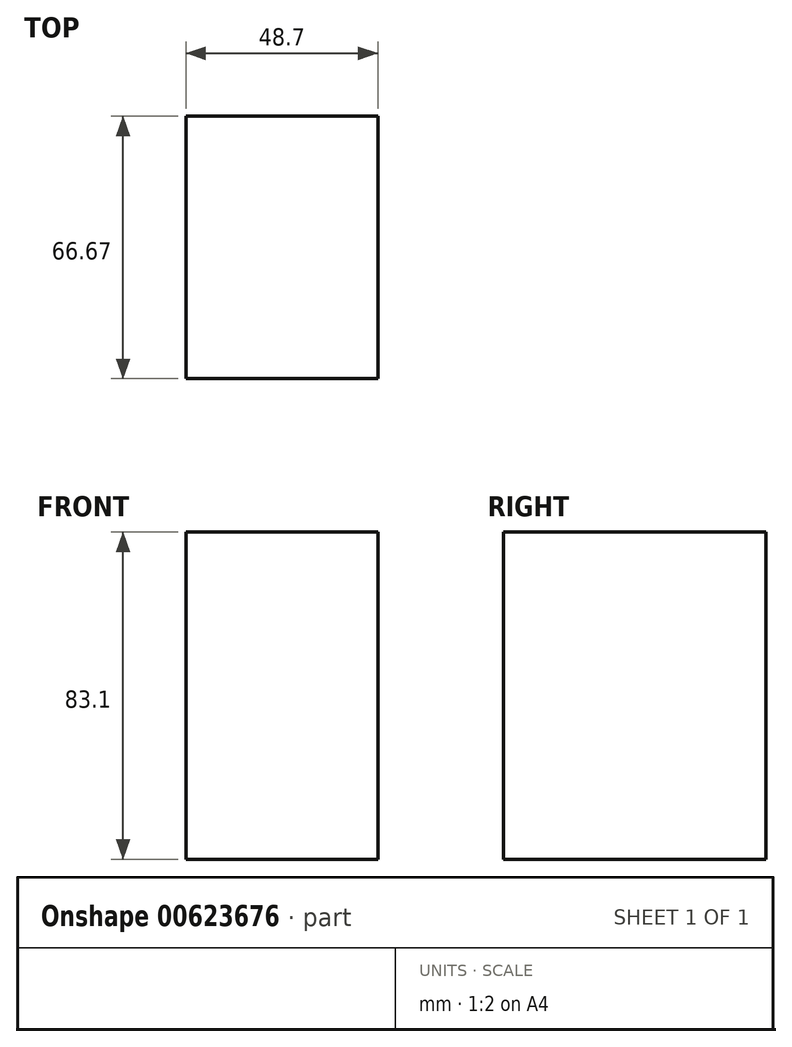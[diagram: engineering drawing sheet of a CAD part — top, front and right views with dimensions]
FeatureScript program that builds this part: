
annotation { "Feature Type Name" : "Feature", "Feature Type Description" : "" }
export const myFeature = defineFeature(function(context is Context, id is Id, definition is map)
    precondition{}
    {
        {
            var Q0;
            Q0=qCreatedBy(makeId("Front.planeOp"),FACE);
            var sketch = newSketch(context, id + "F0", { "sketchPlane" : qUnion([Q0])});
            skLineSegment(sketch, "E0.bottom", {"start": v(0, 0) * mm, "end": v(0, 0) * mm});
            skLineSegment(sketch, "E0.top", {"start": v(0, 0) * mm, "end": v(0, 0) * mm});
            skLineSegment(sketch, "E0.left", {"start": v(0, 0) * mm, "end": v(0, 0) * mm});
            skLineSegment(sketch, "E0.right", {"start": v(0, 0) * mm, "end": v(0, 0) * mm});
            skLineSegment(sketch, "E1.bottom", {"start": v(-48.7, 70.04) * mm, "end": v(0, 70.04) * mm});
            skLineSegment(sketch, "E1.top", {"start": v(-48.7, -13.06) * mm, "end": v(0, -13.06) * mm});
            skLineSegment(sketch, "E1.left", {"start": v(-48.7, 70.04) * mm, "end": v(-48.7, -13.06) * mm});
            skLineSegment(sketch, "E1.right", {"start": v(0, 70.04) * mm, "end": v(0, -13.06) * mm});
            skLineSegment(sketch, "E2.bottom", {"start": v(-83.77, 122.4) * mm, "end": v(-81.56, 122.4) * mm});
            skLineSegment(sketch, "E2.top", {"start": v(-83.77, 116.44) * mm, "end": v(-81.56, 116.44) * mm});
            skLineSegment(sketch, "E2.left", {"start": v(-83.77, 122.4) * mm, "end": v(-83.77, 116.44) * mm});
            skLineSegment(sketch, "E2.right", {"start": v(-81.56, 122.4) * mm, "end": v(-81.56, 116.44) * mm});
            skSolve(sketch);
        }
        {
            var Q0;
            Q0=makeQuery(id+"F0.imprint","IMPRINT",FACE,{"disambiguationData":[TD([[makeQuery(id+"F0.imprint","IMPRINT",EDGE,{"derivedFrom":sQuery(id+"F0.wireOp",EDGE,"E1.bottom")}),-1.0]])]});
            extrude(context, id + "F1", {"entities" : qUnion([Q0]), "depth" : 66.67 * mm, "offsetDistance" : 25.4 * mm});
        }
    });
